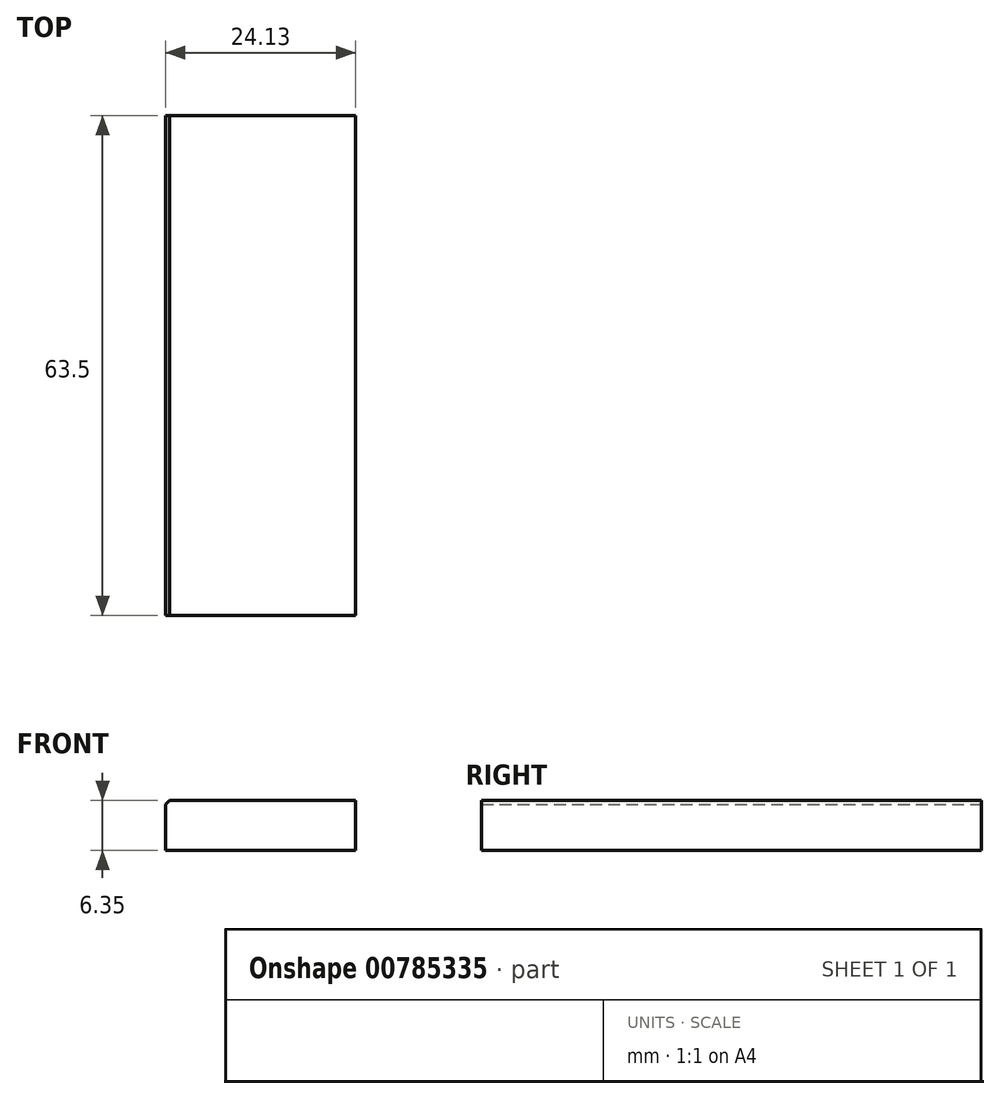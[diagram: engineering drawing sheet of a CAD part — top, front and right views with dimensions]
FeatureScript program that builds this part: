
annotation { "Feature Type Name" : "Feature", "Feature Type Description" : "" }
export const myFeature = defineFeature(function(context is Context, id is Id, definition is map)
    precondition{}
    {
        {
            var Q0;
            Q0=qCreatedBy(makeId("Front.planeOp"),FACE);
            var sketch = newSketch(context, id + "F0", { "sketchPlane" : qUnion([Q0])});
            skLineSegment(sketch, "E0.bottom", {"start": v(4.76, 0) * mm, "end": v(34.93, 0) * mm});
            skLineSegment(sketch, "E0.top", {"start": v(4.76, 12.7) * mm, "end": v(34.93, 12.7) * mm});
            skLineSegment(sketch, "E0.left", {"start": v(0, 4.76) * mm, "end": v(0, 7.94) * mm});
            skLineSegment(sketch, "E0.right", {"start": v(34.93, 0) * mm, "end": v(34.93, 12.7) * mm});
            skLineSegment(sketch, "E1.bottom", {"start": v(34.93, 12.7) * mm, "end": v(10.8, 12.7) * mm});
            skLineSegment(sketch, "E1.top", {"start": v(34.93, 6.35) * mm, "end": v(10.8, 6.35) * mm});
            skLineSegment(sketch, "E1.left", {"start": v(34.93, 12.7) * mm, "end": v(34.93, 6.35) * mm});
            skLineSegment(sketch, "E1.right", {"start": v(10.8, 12.7) * mm, "end": v(10.8, 6.35) * mm});
            skLineSegment(sketch, "E2.bottom", {"start": v(17.46, 0) * mm, "end": v(20.64, 0) * mm});
            skLineSegment(sketch, "E2.top", {"start": v(17.46, 3.18) * mm, "end": v(20.64, 3.18) * mm});
            skLineSegment(sketch, "E2.left", {"start": v(17.46, 0) * mm, "end": v(17.46, 3.18) * mm});
            skLineSegment(sketch, "E2.right", {"start": v(20.64, 0) * mm, "end": v(20.64, 3.18) * mm});
            skPoint(sketch, "E3.visualSharp", {"position": v(0, 12.7) * mm});
            skArc(sketch, "E3.filletArc", {"start": v(4.76, 12.7) * mm, "mid": v(1.4, 11.3) * mm, "end": v(0, 7.94) * mm});
            skPoint(sketch, "E4.visualSharp", {"position": v(0, 0) * mm});
            skArc(sketch, "E4.filletArc", {"start": v(0, 4.76) * mm, "mid": v(1.4, 1.4) * mm, "end": v(4.76, 0) * mm});
            skSolve(sketch);
        }
        {
            var Q0;
            Q0=makeQuery(id+"F0.imprint","IMPRINT",FACE,{"disambiguationData":[TD([[makeQuery(id+"F0.imprint","IMPRINT",EDGE,{"derivedFrom":sQuery(id+"F0.wireOp",EDGE,"E0.top")}),-1.0]])]});
            extrude(context, id + "F1", {"entities" : qUnion([Q0]), "depth" : 63.5 * mm, "offsetDistance" : 25.4 * mm});
        }
        {
            var Q0;
            Q0=makeQuery(id+"F1.opExtrude","SWEPT_EDGE",EDGE,{"disambiguationData":[OSD([sQuery(id+"F0.wireOp",EDGE,"E0.top"),sQuery(id+"F0.wireOp",EDGE,"E1.bottom"),sQuery(id+"F0.wireOp",EDGE,"E1.right")])]});
            chamfer(context, id + "F2", {"entities" : qUnion([Q0]), "width" : 0.5 * mm, "tangentPropagation" : true});
        }
    });
